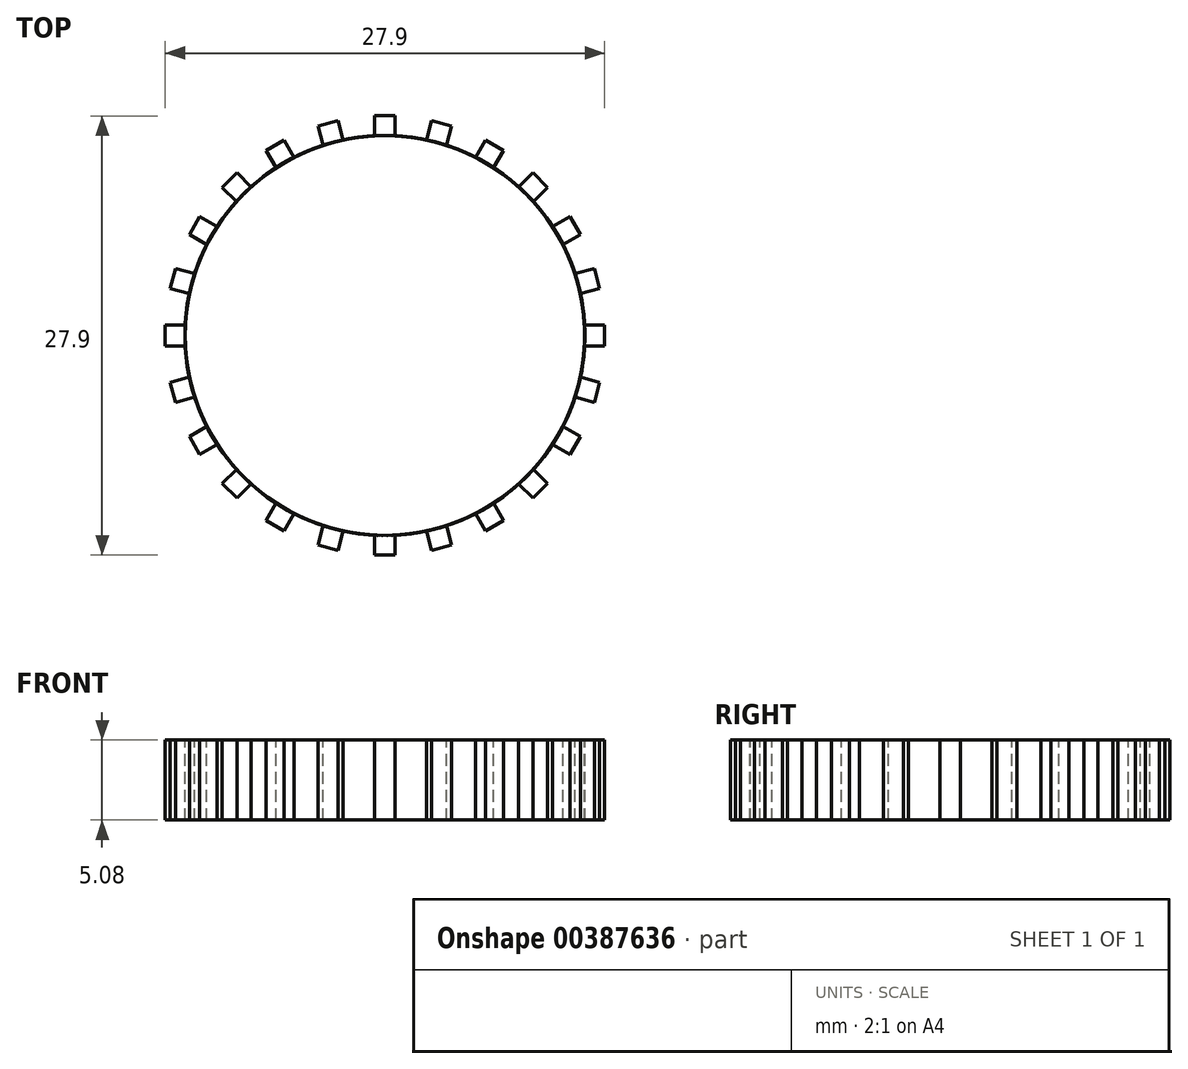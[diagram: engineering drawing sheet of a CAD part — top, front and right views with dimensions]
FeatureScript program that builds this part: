
annotation { "Feature Type Name" : "Feature", "Feature Type Description" : "" }
export const myFeature = defineFeature(function(context is Context, id is Id, definition is map)
    precondition{}
    {
        {
            var Q0;
            Q0=qCreatedBy(makeId("Top.planeOp"),FACE);
            var sketch = newSketch(context, id + "F0", { "sketchPlane" : qUnion([Q0])});
            skArc(sketch, "E0", {"start": v(-0.66, 12.68) * mm, "mid": v(0, -12.7) * mm, "end": v(0.66, 12.68) * mm});
            skLineSegment(sketch, "E1", {"start": v(-0.66, 12.68) * mm, "end": v(-0.66, 13.95) * mm});
            skLineSegment(sketch, "E2", {"start": v(-0.66, 13.95) * mm, "end": v(0, 13.95) * mm});
            skLineSegment(sketch, "E3.MirrorCS", {"start": v(0.66, 13.95) * mm, "end": v(0, 13.95) * mm});
            skLineSegment(sketch, "E4.MirrorCS", {"start": v(0.66, 12.68) * mm, "end": v(0.66, 13.95) * mm});
            skSolve(sketch);
        }
        {
            var Q0;
            Q0=makeQuery(id+"F0.imprint","IMPRINT",FACE,{"disambiguationData":[TD([[makeQuery(id+"F0.imprint","IMPRINT",EDGE,{"derivedFrom":sQuery(id+"F0.wireOp",EDGE,"E0")}),1.0]])]});
            extrude(context, id + "F1", {"entities" : qUnion([Q0]), "oppositeDirection" : true, "depth" : 5.08 * mm, "offsetDistance" : 25.4 * mm});
        }
        {
            var Q0;
            Q0=makeQuery(id+"F1.opExtrude","SWEPT_BODY",BODY,{"disambiguationData":[OSD([sQuery(id+"F0.wireOp",EDGE,"E0"),sQuery(id+"F0.wireOp",EDGE,"E1"),sQuery(id+"F0.wireOp",EDGE,"E2"),sQuery(id+"F0.wireOp",EDGE,"E3.MirrorCS"),sQuery(id+"F0.wireOp",EDGE,"E4.MirrorCS")])]});
            var Q1;
            Q1=makeQuery(id+"F1.opExtrude","SWEPT_FACE",FACE,{"disambiguationData":[OSD([sQuery(id+"F0.wireOp",EDGE,"E0")])]});
            circularPattern(context, id + "F2", {"entities" : qUnion([Q0]), "axis" : qUnion([Q1]), "angle" : 360 * degree, "instanceCount" : 24, "oppositeDirection" : true, "equalSpace" : true});
        }
    });
